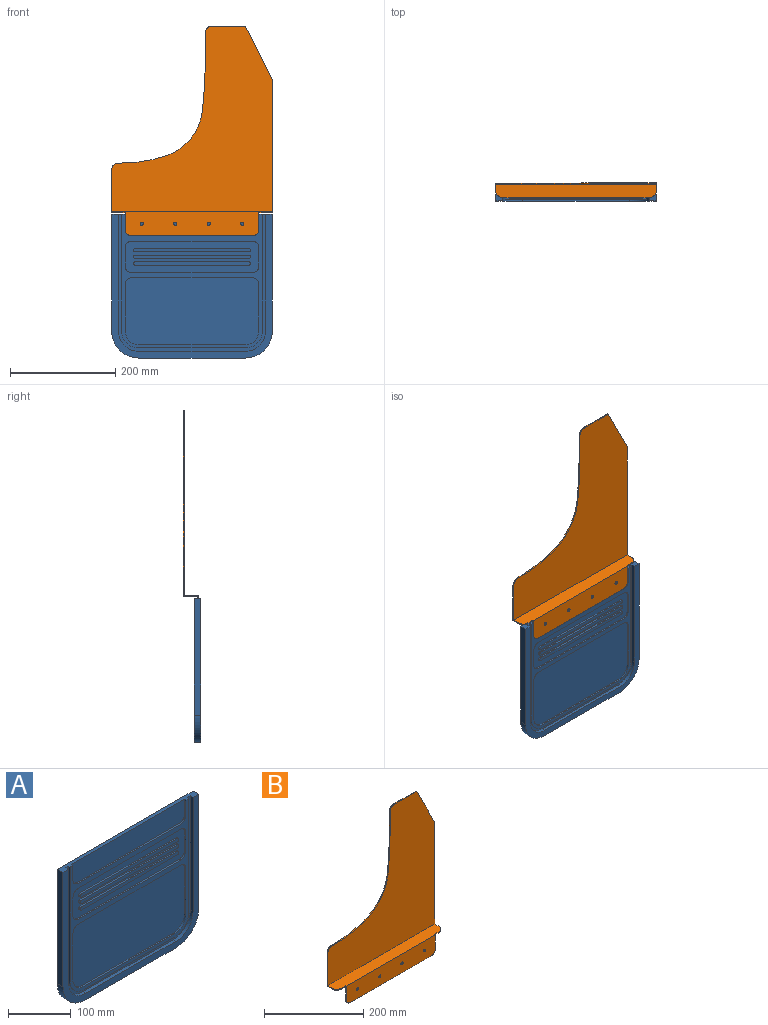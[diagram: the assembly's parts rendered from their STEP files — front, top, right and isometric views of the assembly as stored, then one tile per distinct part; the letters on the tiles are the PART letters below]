
ASSEMBLY  parts=2 mates=1
PART A: 59 faces, bbox 304.8x12.7x273.1 mm
  f0: plane 279.4x260.35mm, normal (0,-1,0), area 4809.6mm2, adj f3,f7,f8,f15,f16,f17,f18,f29
  f1: plane 254x41.28mm, normal (0,-1,0), area 10414.6mm2, adj f5,f6,f26,f27,f28,f58
  f2: plane 222.25x12.7mm, normal (1,0,0), area 2822.6mm2, adj f4,f12,f14,f58
  f3: plane 222.25x6.35mm, normal (-1,0,0), area 1411.3mm2, adj f0,f4,f15,f58
  f4: plane 304.8x273.05mm, normal (0,-1,0), area 9999.3mm2, adj f2,f3,f10,f11,f13,f14,f15,f16
  f5: plane 28.58x3.18mm, normal (-1,0,0), area 90.7mm2, adj f1,f9,f26,f58
  f6: plane 28.58x3.18mm, normal (1,0,0), area 90.7mm2, adj f1,f9,f28,f58
  f7: plane 222.25x3.18mm, normal (-1,0,0), area 705.6mm2, adj f0,f9,f29,f58
  f8: plane 222.25x3.18mm, normal (1,0,0), area 705.6mm2, adj f0,f9,f31,f58
  f9: plane 266.7x254mm, normal (0,-1,0), area 9798.5mm2, adj f5,f6,f7,f8,f19,f20,f21,f22
  f10: plane 222.25x12.7mm, normal (-1,0,0), area 2822.6mm2, adj f4,f12,f13,f58
  f11: plane 203.2x12.7mm, normal (0,0,-1), area 2580.6mm2, adj f4,f12,f13,f14
  f12: plane 304.8x273.05mm, normal (0,1,0), area 82118mm2, adj f2,f10,f11,f13,f14,f58
  f13: cylinder r=50.8mm len=50.8mm, axis (0,-1,0), area 1013.4mm2, adj f4,f10,f11,f12
  f14: cylinder r=50.8mm len=50.8mm, axis (0,1,0), area 1013.4mm2, adj f2,f4,f11,f12
  f15: cylinder r=38.1mm len=38.1mm, axis (0,1,0), area 380mm2, adj f0,f3,f4,f16
  f16: plane 203.2x6.35mm, normal (0,0,1), area 1290.3mm2, adj f0,f4,f15,f17
  f17: cylinder r=38.1mm len=38.1mm, axis (0,1,0), area 380mm2, adj f0,f4,f16,f18
  f18: plane 222.25x6.35mm, normal (1,0,0), area 1411.3mm2, adj f0,f4,f17,f58
  f19: cylinder r=12.7mm len=12.7mm, axis (0,1,0), area 63.3mm2, adj f9,f20,f40,f42
  f20: plane 228.6x3.18mm, normal (0,0,-1), area 725.8mm2, adj f9,f19,f21,f42
  f21: cylinder r=12.7mm len=12.7mm, axis (0,1,0), area 63.3mm2, adj f9,f20,f22,f42
  f22: plane 88.9x3.18mm, normal (-1,0,0), area 282.3mm2, adj f9,f21,f23,f42
  f23: cylinder r=25.4mm len=25.4mm, axis (0,1,0), area 126.7mm2, adj f9,f22,f24,f42
  f24: plane 203.2x3.18mm, normal (0,0,1), area 645.2mm2, adj f9,f23,f25,f42
  f25: cylinder r=25.4mm len=25.4mm, axis (0,1,0), area 126.7mm2, adj f9,f24,f40,f42
  f26: cylinder r=12.7mm len=12.7mm, axis (0,1,0), area 63.3mm2, adj f1,f5,f9,f27
  f27: plane 228.6x3.18mm, normal (0,0,1), area 725.8mm2, adj f1,f9,f26,f28
  f28: cylinder r=12.7mm len=12.7mm, axis (0,1,0), area 63.3mm2, adj f1,f6,f9,f27
  f29: cylinder r=31.75mm len=31.75mm, axis (0,1,0), area 158.3mm2, adj f0,f7,f9,f30
  f30: plane 203.2x3.18mm, normal (0,0,-1), area 645.2mm2, adj f0,f9,f29,f31
  f31: cylinder r=31.75mm len=31.75mm, axis (0,1,0), area 158.3mm2, adj f0,f8,f9,f30
  f32: cylinder r=12.7mm len=12.7mm, axis (0,1,0), area 63.3mm2, adj f9,f33,f39,f41
  f33: plane 228.6x3.18mm, normal (0,0,-1), area 725.8mm2, adj f9,f32,f34,f41
  f34: cylinder r=12.7mm len=12.7mm, axis (0,1,0), area 63.3mm2, adj f9,f33,f35,f41
  f35: plane 34.93x3.18mm, normal (-1,0,0), area 110.9mm2, adj f9,f34,f36,f41
  f36: cylinder r=12.7mm len=12.7mm, axis (0,1,0), area 63.3mm2, adj f9,f35,f37,f41
  f37: plane 228.6x3.18mm, normal (0,0,1), area 725.8mm2, adj f9,f36,f38,f41
  f38: cylinder r=12.7mm len=12.7mm, axis (0,1,0), area 63.3mm2, adj f9,f37,f39,f41
  f39: plane 34.93x3.18mm, normal (1,0,0), area 110.9mm2, adj f9,f32,f38,f41
  f40: plane 88.9x3.18mm, normal (1,0,0), area 282.3mm2, adj f9,f19,f25,f42
  f41: plane 254x60.33mm, normal (0,-1,0), area 10976.2mm2, adj f32,f33,f34,f35,f36,f37,f38,f39
  f42: plane 254x127mm, normal (0,-1,0), area 31911.9mm2, adj f19,f20,f21,f22,f23,f24,f25,f40
  f43: plane 215.9x3.18mm, normal (0,0,1), area 685.5mm2, adj f41,f44,f46,f47
  f44: cylinder r=3.17mm len=6.35mm, axis (0,1,0), area 31.7mm2, adj f41,f43,f45,f47
  f45: plane 215.9x3.18mm, normal (0,0,-1), area 685.5mm2, adj f41,f44,f46,f47
  f46: cylinder r=3.17mm len=6.35mm, axis (0,1,0), area 31.7mm2, adj f41,f43,f45,f47
  f47: plane 222.25x6.35mm, normal (0,-1,0), area 1402.6mm2, adj f43,f44,f45,f46
  f48: plane 215.9x3.18mm, normal (0,0,1), area 685.5mm2, adj f41,f49,f51,f52
  f49: cylinder r=3.17mm len=6.35mm, axis (0,1,0), area 31.7mm2, adj f41,f48,f50,f52
  f50: plane 215.9x3.18mm, normal (0,0,-1), area 685.5mm2, adj f41,f49,f51,f52
  f51: cylinder r=3.17mm len=6.35mm, axis (0,1,0), area 31.7mm2, adj f41,f48,f50,f52
  f52: plane 222.25x6.35mm, normal (0,-1,0), area 1402.6mm2, adj f48,f49,f50,f51
  f53: plane 215.9x3.18mm, normal (0,0,1), area 685.5mm2, adj f41,f54,f56,f57
  f54: cylinder r=3.17mm len=6.35mm, axis (0,1,0), area 31.7mm2, adj f41,f53,f55,f57
  f55: plane 215.9x3.18mm, normal (0,0,-1), area 685.5mm2, adj f41,f54,f56,f57
  f56: cylinder r=3.17mm len=6.35mm, axis (0,1,0), area 31.7mm2, adj f41,f53,f55,f57
  f57: plane 222.25x6.35mm, normal (0,-1,0), area 1402.6mm2, adj f53,f54,f55,f56
  f58: plane 304.8x12.7mm, normal (0,0,1), area 2137.1mm2, adj f0,f1,f2,f3,f4,f5,f6,f7
PART B: 30 faces, bbox 304.8x29.5x398.9 mm
  f0: plane 12.7x2.03mm, normal (0,-1,0), area 25.8mm2, adj f14,f15,f18,f23
  f1: cylinder r=101.6mm len=85.79mm, axis (0,1,0), area 235.1mm2, adj f2,f9,f10,f11
  f2: cylinder r=262.16mm len=85.07mm, axis (0,1,0), area 176mm2, adj f1,f3,f10,f11
  f3: plane 6.35x2.03mm, normal (0,0,1), area 12.9mm2, adj f2,f10,f11,f12
  f4: plane 81.41x14.73mm, normal (-1,0,0), area 191.2mm2, adj f10,f11,f12,f14,f15,f23
  f5: plane 252.86x14.73mm, normal (1,0,0), area 539.6mm2, adj f6,f10,f11,f14,f15,f22
  f6: plane 101.6x50.8mm, normal (0.89,0,0.45), area 230.8mm2, adj f5,f7,f10,f11
  f7: plane 63.5x2.03mm, normal (0,0,1), area 129mm2, adj f6,f10,f11,f13
  f8: plane 38.1x2.03mm, normal (-1,0,0), area 77.4mm2, adj f9,f10,f11,f13
  f9: cylinder r=1079.5mm len=109.58mm, axis (0,1,0), area 223mm2, adj f1,f8,f10,f11
  f10: plane 352.43x304.8mm, normal (0,-1,0), area 62335.1mm2, adj f1,f2,f3,f4,f5,f6,f7,f8
  f11: plane 354.46x304.8mm, normal (0,1,0), area 62954.5mm2, adj f1,f2,f3,f4,f5,f6,f7,f8
  f12: cylinder r=12.7mm len=12.7mm, axis (0,-1,0), area 40.5mm2, adj f3,f4,f10,f11
  f13: cylinder r=12.7mm len=12.7mm, axis (0,1,0), area 40.5mm2, adj f7,f8,f10,f11
  f14: plane 304.8x27.43mm, normal (0,0,1), area 8188.8mm2, adj f0,f4,f5,f10,f16,f18,f20,f21
  f15: plane 304.8x27.43mm, normal (0,0,-1), area 8292mm2, adj f0,f4,f5,f11,f16,f17,f22,f23
  f16: plane 12.7x2.03mm, normal (0,-1,0), area 25.8mm2, adj f14,f15,f20,f22
  f17: plane 254x44.45mm, normal (0,1,0), area 11094.4mm2, adj f15,f18,f19,f20,f24,f25,f26,f27
  f18: plane 33.78x2.03mm, normal (-1,0,0), area 68.6mm2, adj f0,f14,f17,f21,f24
  f19: plane 228.6x2.03mm, normal (0,0,-1), area 464.5mm2, adj f17,f21,f24,f25
  f20: plane 33.78x2.03mm, normal (1,0,0), area 68.6mm2, adj f14,f16,f17,f21,f25
  f21: plane 254x46.48mm, normal (0,-1,0), area 11610.5mm2, adj f14,f18,f19,f20,f24,f25,f26,f27
  f22: cylinder r=12.7mm len=12.7mm, axis (0,0,-1), area 40.5mm2, adj f5,f14,f15,f16
  f23: cylinder r=12.7mm len=12.7mm, axis (0,0,-1), area 40.5mm2, adj f0,f4,f14,f15
  f24: cylinder r=12.7mm len=12.7mm, axis (0,1,0), area 40.5mm2, adj f17,f18,f19,f21
  f25: cylinder r=12.7mm len=12.7mm, axis (0,-1,0), area 40.5mm2, adj f17,f19,f20,f21
  f26: cylinder r=3.17mm len=6.35mm, axis (0,-1,0), area 40.5mm2, adj f17,f21
  f27: cylinder r=3.17mm len=6.35mm, axis (0,-1,0), area 40.5mm2, adj f17,f21
  f28: cylinder r=3.17mm len=6.35mm, axis (0,-1,0), area 40.5mm2, adj f17,f21
  f29: cylinder r=3.17mm len=6.35mm, axis (0,-1,0), area 40.5mm2, adj f17,f21
PLACE A t=(-152.4,12.7,0)mm fixed
PLACE B t=(-152.4,33.78,278.26)mm
MATE fastened B.f17 <-> A.f1  axis (0,1,0) through (0,6.35,231.78)mm
